# Revit family: Console Lavatory_TOTO_PJS01
name_source: partatom
category: 衛生器具
revit_build: Autodesk Revit 2018 (Build: 20181011_1500(x64)
units: mm (PartAtom-declared; Revit-internal decimal feet)

## family parameters
OmniClass タイトル = Sanitary, Laundry, and Cleaning Equipment
OmniClass 番号 = 23.45.00.00
パーツ タイプ = 標準
ロード時にボイドで切り取り = いいえ
丸型コネクタ寸法 = 直径を使用
作業面ベース = いいえ
共有 = いいえ
常に垂直 = はい
部屋計算ポイント = いいえ

## types (1)
- Console Lavatory_TOTO_PJS01
    Finish = basin_material
    Height = 165
    Length = 404
    TOTO AsiaOceania = PJS01WE
    TOTO AsiaOceania URL = https://www.twtoto.com.tw
    TOTO China = PJS01W
    TOTO China URL = http://www.toto.com.cn
    TOTO HongKong = PJS01WE
    TOTO HongKong URL = http://hk.toto.com
    TOTO India = PJS01WE
    TOTO India URL = https://in.toto.com
    TOTO Korea = PJS01W
    TOTO Korea URL = https://kr.toto.com
    TOTO Taiwan = PJS01WE
    TOTO Taiwan URL = https://www.twtoto.com.tw
    TOTO Vietnam = PJS01WE
    TOTO Vietnam URL = https://vn.toto.com
    Width = 632
    排気配管 = いいえ
    排水配管 = いいえ
    水配管 = いいえ
    温水配管 = いいえ
    製造元 = TOTO Ltd.
    説明 = Console Lavatory/桌上式洗脸盆

## geometry (parser evidence)
native form markers: Sweep x2
no freeform markers — native parametric forms only
